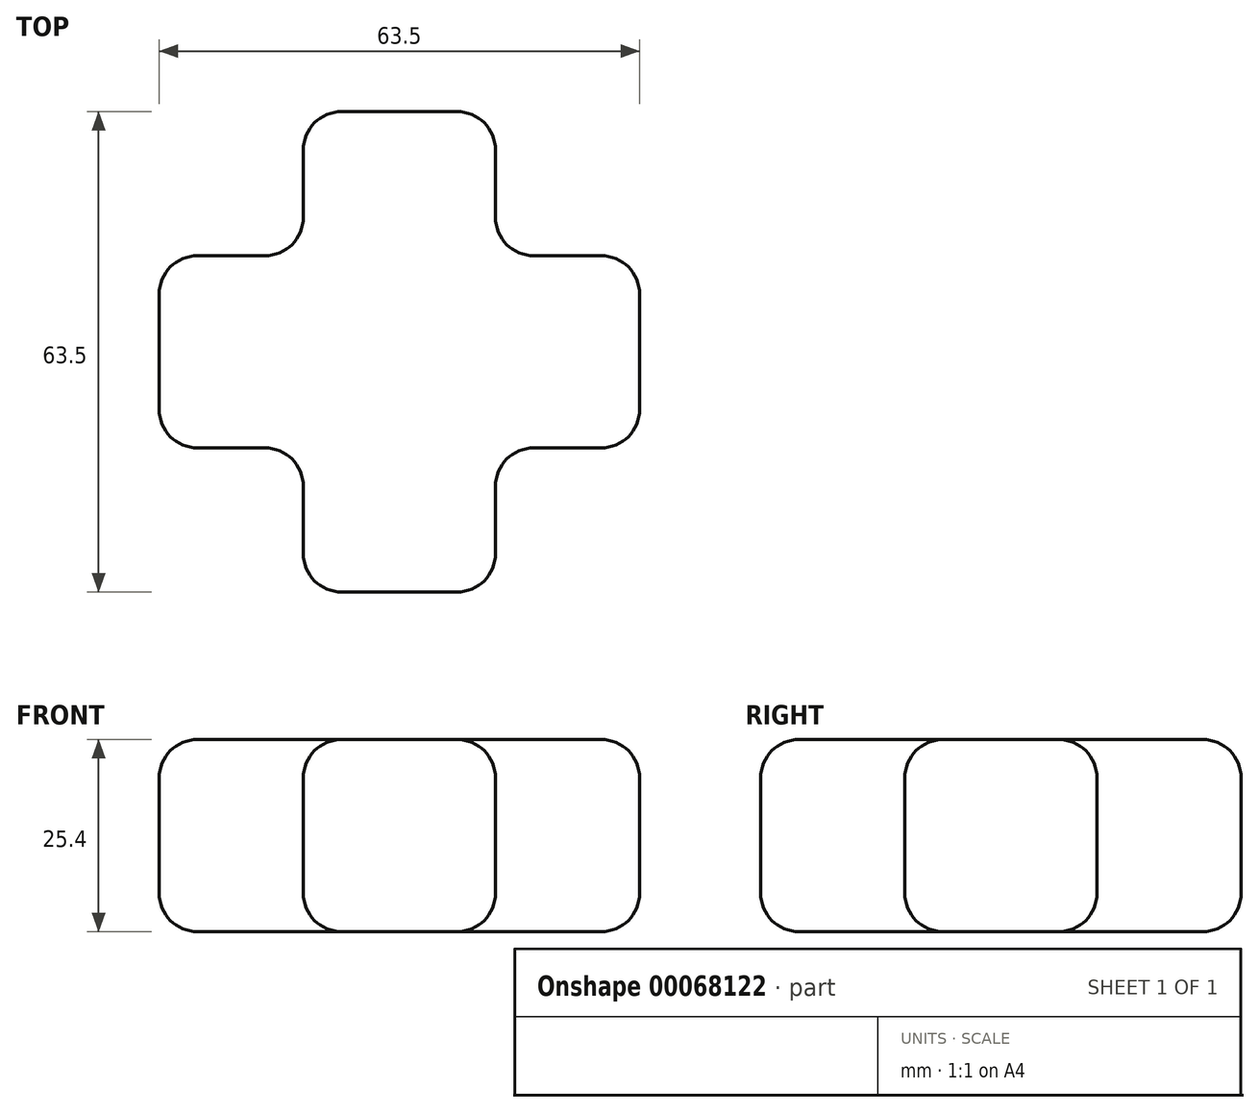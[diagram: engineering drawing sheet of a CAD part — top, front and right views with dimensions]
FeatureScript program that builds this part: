
annotation { "Feature Type Name" : "Feature", "Feature Type Description" : "" }
export const myFeature = defineFeature(function(context is Context, id is Id, definition is map)
    precondition{}
    {
        {
            var Q0;
            Q0=qCreatedBy(makeId("Top.planeOp"),FACE);
            var sketch = newSketch(context, id + "F0", { "sketchPlane" : qUnion([Q0])});
            skLineSegment(sketch, "E0.bottom", {"start": v(0, 0) * mm, "end": v(19.05, 0) * mm});
            skLineSegment(sketch, "E0.top", {"start": v(0, 25.4) * mm, "end": v(19.05, 25.4) * mm});
            skLineSegment(sketch, "E0.left", {"start": v(0, 0) * mm, "end": v(0, 25.4) * mm});
            skLineSegment(sketch, "E0.right", {"start": v(63.5, 0) * mm, "end": v(63.5, 25.4) * mm});
            skLineSegment(sketch, "E1.bottom", {"start": v(19.05, 44.45) * mm, "end": v(44.45, 44.45) * mm});
            skLineSegment(sketch, "E1.top", {"start": v(19.05, -19.05) * mm, "end": v(44.45, -19.05) * mm});
            skLineSegment(sketch, "E1.left", {"start": v(19.05, 44.45) * mm, "end": v(19.05, 25.4) * mm});
            skLineSegment(sketch, "E1.right", {"start": v(44.45, 44.45) * mm, "end": v(44.45, 25.4) * mm});
            skLineSegment(sketch, "E2.trimOffspring", {"start": v(44.45, 25.4) * mm, "end": v(63.5, 25.4) * mm});
            skLineSegment(sketch, "E3.trimOffspring", {"start": v(44.45, 0) * mm, "end": v(44.45, -19.05) * mm});
            skLineSegment(sketch, "E4.trimOffspring", {"start": v(44.45, 0) * mm, "end": v(63.5, 0) * mm});
            skLineSegment(sketch, "E5.trimOffspring", {"start": v(19.05, 0) * mm, "end": v(19.05, -19.05) * mm});
            skSolve(sketch);
        }
        {
            var Q0;
            Q0=makeQuery(id+"F0.imprint","IMPRINT",FACE,{"disambiguationData":[TD([[makeQuery(id+"F0.imprint","IMPRINT",EDGE,{"derivedFrom":sQuery(id+"F0.wireOp",EDGE,"E0.bottom")}),1.0]])]});
            extrude(context, id + "F1", {"entities" : qUnion([Q0]), "depth" : 25.4 * mm});
        }
        {
            var Q0;
            Q0=makeQuery(id+"F1.opExtrude","CAP_FACE",FACE,{"disambiguationData":[OSD([sQuery(id+"F0.wireOp",EDGE,"E0.bottom"),sQuery(id+"F0.wireOp",EDGE,"E0.top"),sQuery(id+"F0.wireOp",EDGE,"E0.left"),sQuery(id+"F0.wireOp",EDGE,"E0.right"),sQuery(id+"F0.wireOp",EDGE,"E1.bottom"),sQuery(id+"F0.wireOp",EDGE,"E1.top"),sQuery(id+"F0.wireOp",EDGE,"E1.left"),sQuery(id+"F0.wireOp",EDGE,"E1.right"),sQuery(id+"F0.wireOp",EDGE,"E2.trimOffspring"),sQuery(id+"F0.wireOp",EDGE,"E3.trimOffspring"),sQuery(id+"F0.wireOp",EDGE,"E4.trimOffspring"),sQuery(id+"F0.wireOp",EDGE,"E5.trimOffspring")])],"isStart":false});
            var Q1;
            Q1=makeQuery(id+"F1.opExtrude","CAP_FACE",FACE,{"disambiguationData":[OSD([sQuery(id+"F0.wireOp",EDGE,"E0.bottom"),sQuery(id+"F0.wireOp",EDGE,"E0.top"),sQuery(id+"F0.wireOp",EDGE,"E0.left"),sQuery(id+"F0.wireOp",EDGE,"E0.right"),sQuery(id+"F0.wireOp",EDGE,"E1.bottom"),sQuery(id+"F0.wireOp",EDGE,"E1.top"),sQuery(id+"F0.wireOp",EDGE,"E1.left"),sQuery(id+"F0.wireOp",EDGE,"E1.right"),sQuery(id+"F0.wireOp",EDGE,"E2.trimOffspring"),sQuery(id+"F0.wireOp",EDGE,"E3.trimOffspring"),sQuery(id+"F0.wireOp",EDGE,"E4.trimOffspring"),sQuery(id+"F0.wireOp",EDGE,"E5.trimOffspring")])],"isStart":true});
            var Q2;
            Q2=makeQuery(id+"F1.opExtrude","SWEPT_FACE",FACE,{"disambiguationData":[OSD([sQuery(id+"F0.wireOp",EDGE,"E1.bottom")])]});
            var Q3;
            Q3=makeQuery(id+"F1.opExtrude","SWEPT_FACE",FACE,{"disambiguationData":[OSD([sQuery(id+"F0.wireOp",EDGE,"E0.top")])]});
            var Q4;
            Q4=makeQuery(id+"F1.opExtrude","SWEPT_FACE",FACE,{"disambiguationData":[OSD([sQuery(id+"F0.wireOp",EDGE,"E2.trimOffspring")])]});
            var Q5;
            Q5=makeQuery(id+"F1.opExtrude","SWEPT_FACE",FACE,{"disambiguationData":[OSD([sQuery(id+"F0.wireOp",EDGE,"E0.right")])]});
            var Q6;
            Q6=makeQuery(id+"F1.opExtrude","SWEPT_FACE",FACE,{"disambiguationData":[OSD([sQuery(id+"F0.wireOp",EDGE,"E3.trimOffspring")])]});
            var Q7;
            Q7=makeQuery(id+"F1.opExtrude","SWEPT_FACE",FACE,{"disambiguationData":[OSD([sQuery(id+"F0.wireOp",EDGE,"E5.trimOffspring")])]});
            var Q8;
            Q8=makeQuery(id+"F1.opExtrude","SWEPT_FACE",FACE,{"disambiguationData":[OSD([sQuery(id+"F0.wireOp",EDGE,"E0.left")])]});
            fillet(context, id + "F2", {"entities" : qUnion([Q0, Q1, Q2, Q3, Q4, Q5, Q6, Q7, Q8]), "radius" : 5.08 * mm, "tangentPropagation" : true, "allowEdgeOverflow" : false});
        }
    });
